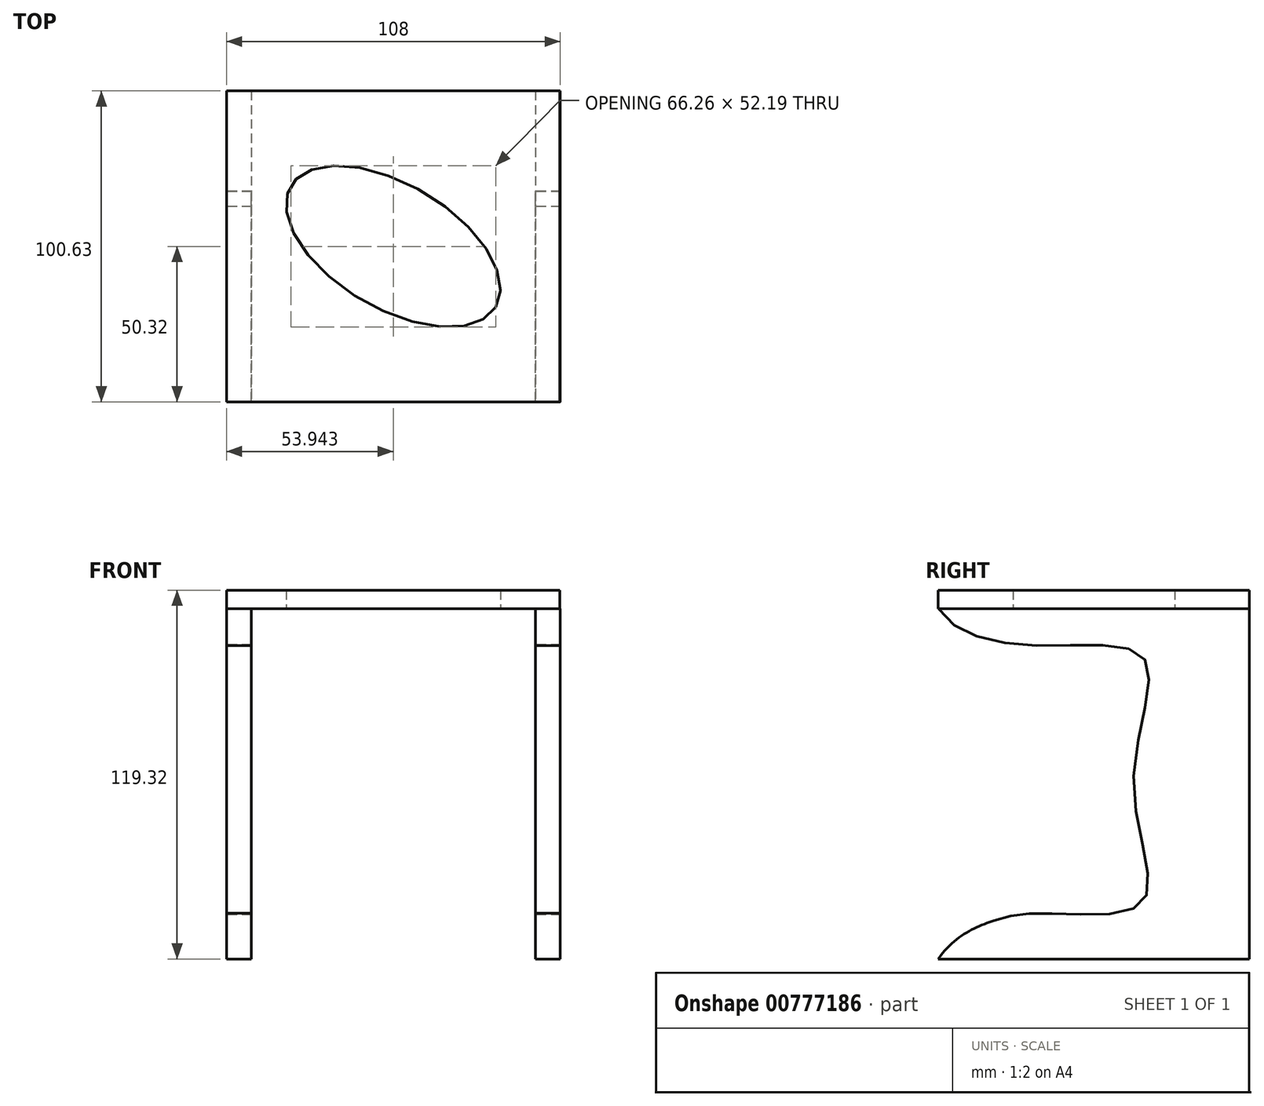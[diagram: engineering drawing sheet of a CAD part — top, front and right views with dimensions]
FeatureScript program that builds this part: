
annotation { "Feature Type Name" : "Feature", "Feature Type Description" : "" }
export const myFeature = defineFeature(function(context is Context, id is Id, definition is map)
    precondition{}
    {
        {
            var Q0;
            Q0=qCreatedBy(makeId("Right.planeOp"),FACE);
            var sketch = newSketch(context, id + "F0", { "sketchPlane" : qUnion([Q0])});
            skLineSegment(sketch, "E0.bottom", {"start": v(50.3, -56.66) * mm, "end": v(-50.3, -56.66) * mm});
            skLineSegment(sketch, "E0.top", {"start": v(50.3, 56.66) * mm, "end": v(-50.3, 56.66) * mm});
            skLineSegment(sketch, "E0.left", {"start": v(50.3, -56.66) * mm, "end": v(50.3, 56.66) * mm});
            skLineSegment(sketch, "E0.right", {"start": v(-50.3, -56.66) * mm, "end": v(-50.3, 56.66) * mm});
            skPoint(sketch, "E0.middle", {"position": v(0, 0) * mm});
            skFitSpline(sketch, "E1", {"points": [v(-50.3, 56.83) * mm, v(-20.83, 44.87) * mm, v(16.23, 40.66) * mm, v(12.86, 0) * mm, v(15.89, -38.17) * mm, v(-15.1, -41.88) * mm, v(-32.29, -44.23) * mm, v(-50.3, -56.66) * mm], "startDerivative": vector(98.67, -160.35) * mm, "endDerivative": vector(-126.02, -184.36) * mm});
            skFitSpline(sketch, "E2", {"points": [v(-32.29, -44.23) * mm, v(-36.33, -31.43) * mm], "startDerivative": vector(-4.38, 4.04) * mm, "endDerivative": vector(-4.38, 4.04) * mm});
            skSolve(sketch);
        }
        {
            var Q0;
            {var subQ5=sQuery(id+"F0.wireOp",EDGE,"E0.bottom");Q0=makeQuery(id+"F0.imprint","IMPRINT",FACE,{"disambiguationData":[TD([[makeQuery(id+"F0.imprint","IMPRINT",EDGE,{"derivedFrom":subQ5}),-1.0]])]});}
            extrude(context, id + "F1", {"entities" : qUnion([Q0]), "depth" : 8 * mm, "offsetDistance" : 25.4 * mm});
        }
        {
            var Q0;
            Q0=makeQuery(id+"F1.opExtrude","SWEPT_BODY",BODY,{"disambiguationData":[OSD([sQuery(id+"F0.wireOp",EDGE,"E0.bottom"),sQuery(id+"F0.wireOp",EDGE,"E0.top"),sQuery(id+"F0.wireOp",EDGE,"E0.left"),sQuery(id+"F0.wireOp",EDGE,"E1")])]});
            transform(context, id + "F2", {"entities" : qUnion([Q0]), "transformType" : TransformType.TRANSLATION_3D, "dx" : 100 * mm, "dy" : 0 * mm, "dz" : 0 * mm, "makeCopy" : true});
        }
        {
            var Q0;
            Q0=makeQuery(id+"F1.opExtrude","SWEPT_FACE",FACE,{"disambiguationData":[OSD([sQuery(id+"F0.wireOp",EDGE,"E0.top")])]});
            var sketch = newSketch(context, id + "F3", { "sketchPlane" : qUnion([Q0])});
            skLineSegment(sketch, "E3.bottom", {"start": v(0, 50.3) * mm, "end": v(107.89, 50.3) * mm});
            skLineSegment(sketch, "E3.top", {"start": v(0, -50.32) * mm, "end": v(107.89, -50.32) * mm});
            skLineSegment(sketch, "E3.left", {"start": v(0, 50.3) * mm, "end": v(0, -50.32) * mm});
            skLineSegment(sketch, "E3.right", {"start": v(107.89, 50.3) * mm, "end": v(107.89, -50.32) * mm});
            skSolve(sketch);
        }
        {
            var Q0;
            Q0 = qSketchRegion(id + "F3", true);
            extrude(context, id + "F4", {"entities" : qUnion([Q0]), "depth" : 6 * mm, "offsetDistance" : 25.4 * mm});
        }
        {
            var Q0;
            Q0=makeQuery(id+"F4.opExtrude","CAP_FACE",FACE,{"disambiguationData":[OSD([sQuery(id+"F3.wireOp",EDGE,"E3.bottom"),sQuery(id+"F3.wireOp",EDGE,"E3.top"),sQuery(id+"F3.wireOp",EDGE,"E3.left"),sQuery(id+"F3.wireOp",EDGE,"E3.right")])],"isStart":false});
            var sketch = newSketch(context, id + "F5", { "sketchPlane" : qUnion([Q0])});
            skLineSegment(sketch, "E4", {"start": v(53.94, 50.3) * mm, "end": v(53.94, -50.32) * mm, "construction": true});
            skLineSegment(sketch, "E5", {"start": v(0, 0) * mm, "end": v(107.89, 0) * mm});
            skEllipse(sketch, "E6", {"center": v(53.94, 0) * mm, "majorRadius": 38.5 * mm, "minorRadius": 20.08 * mm, "majorAxis": v(0.86, -0.5)});
            skSolve(sketch);
        }
        {
            var Q0;
            {var subQ0=sQuery(id+"F5.wireOp",EDGE,"E6");var subQ1=sQuery(id+"F5.wireOp",EDGE,"E5");var subQ2=makeQuery(id+"F5.imprint","INTERSECT",VERTEX,{"disambiguationData":[OD(0.0)],"derivedFrom":[subQ1,subQ0]});Q0=makeQuery(id+"F5.imprint","IMPRINT",FACE,{"disambiguationData":[TD([[makeQuery(id+"F5.imprint","IMPRINT",EDGE,{"disambiguationData":[TD([[subQ2,-1.0]])],"derivedFrom":subQ1}),-1.0]])]});}
            var Q1;
            {var subQ0=sQuery(id+"F5.wireOp",EDGE,"E6");var subQ1=sQuery(id+"F5.wireOp",EDGE,"E5");var subQ2=makeQuery(id+"F5.imprint","INTERSECT",VERTEX,{"disambiguationData":[OD(0.0)],"derivedFrom":[subQ1,subQ0]});Q1=makeQuery(id+"F5.imprint","IMPRINT",FACE,{"disambiguationData":[TD([[makeQuery(id+"F5.imprint","IMPRINT",EDGE,{"disambiguationData":[TD([[subQ2,-1.0]])],"derivedFrom":subQ1}),1.0]])]});}
            extrude(context, id + "F6", {"entities" : qUnion([Q0, Q1]), "operationType" : NewBodyOperationType.REMOVE, "oppositeDirection" : true, "depth" : 25.4 * mm, "offsetDistance" : 25.4 * mm});
        }
    });
